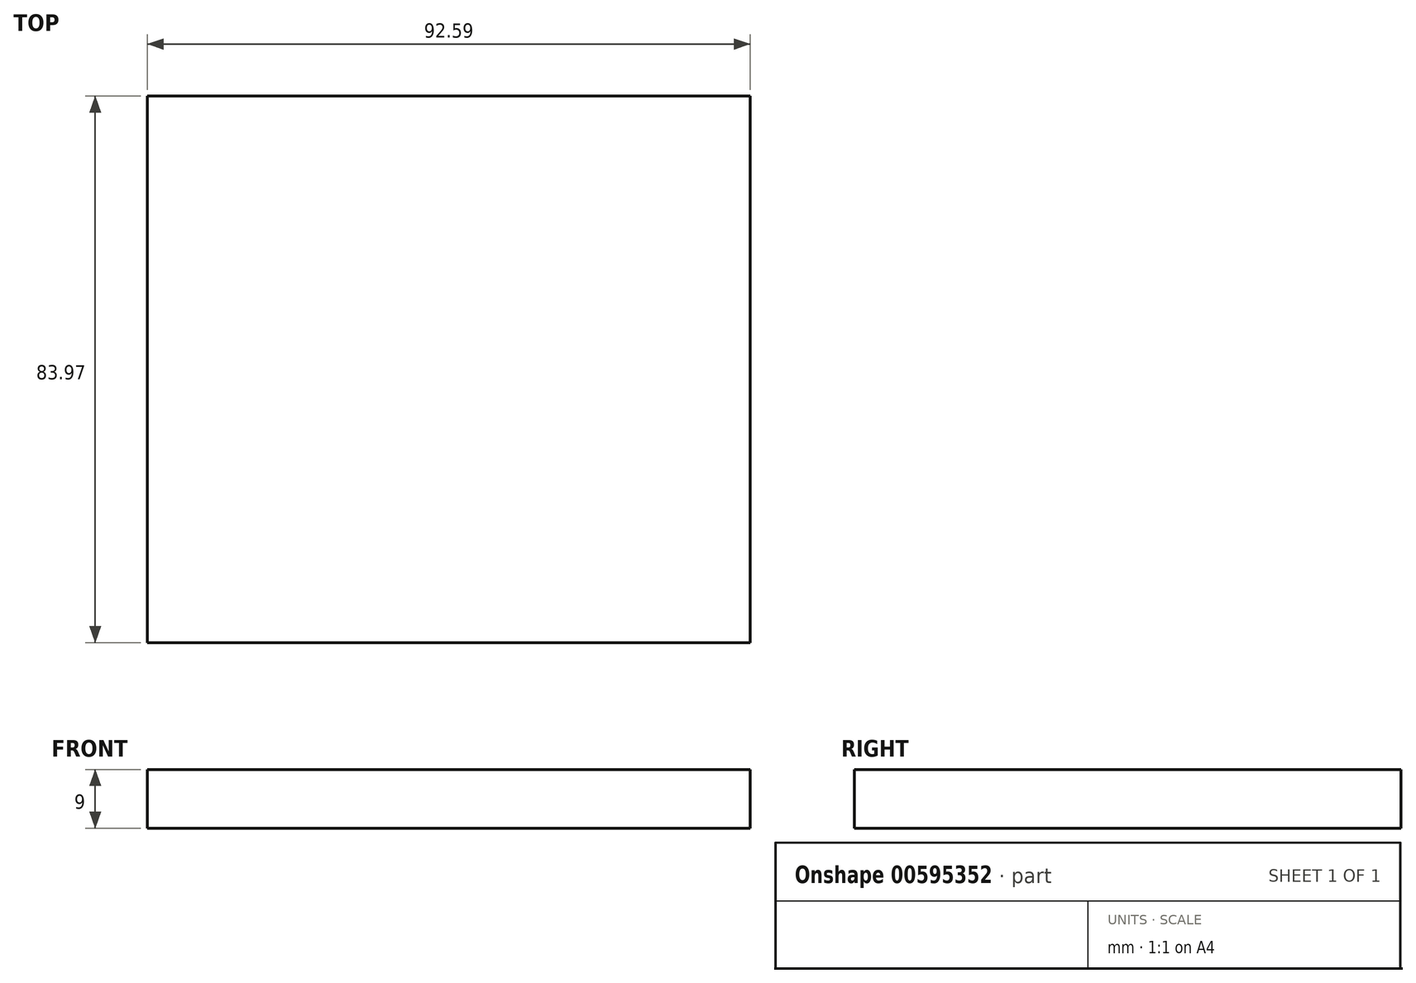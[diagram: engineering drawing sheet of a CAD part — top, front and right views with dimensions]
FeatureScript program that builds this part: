
annotation { "Feature Type Name" : "Feature", "Feature Type Description" : "" }
export const myFeature = defineFeature(function(context is Context, id is Id, definition is map)
    precondition{}
    {
        {
            var Q0;
            Q0=qCreatedBy(makeId("Top.planeOp"),FACE);
            var sketch = newSketch(context, id + "F0", { "sketchPlane" : qUnion([Q0])});
            skLineSegment(sketch, "E0.bottom", {"start": v(-43.8, 44.48) * mm, "end": v(48.8, 44.48) * mm});
            skLineSegment(sketch, "E0.top", {"start": v(-43.8, -39.49) * mm, "end": v(48.8, -39.49) * mm});
            skLineSegment(sketch, "E0.left", {"start": v(-43.8, 44.48) * mm, "end": v(-43.8, -39.49) * mm});
            skLineSegment(sketch, "E0.right", {"start": v(48.8, 44.48) * mm, "end": v(48.8, -39.49) * mm});
            skSolve(sketch);
        }
        {
            var Q0;
            Q0 = qSketchRegion(id + "F0", true);
            var Q1;
            Q1=makeQuery(id+"F0.imprint","IMPRINT",FACE,{"disambiguationData":[TD([[makeQuery(id+"F0.imprint","IMPRINT",EDGE,{"derivedFrom":sQuery(id+"F0.wireOp",EDGE,"E0.bottom")}),-1.0]])]});
            extrude(context, id + "F1", {"entities" : qUnion([Q0, Q1]), "depth" : 9 * mm, "offsetDistance" : 25 * mm});
        }
    });
